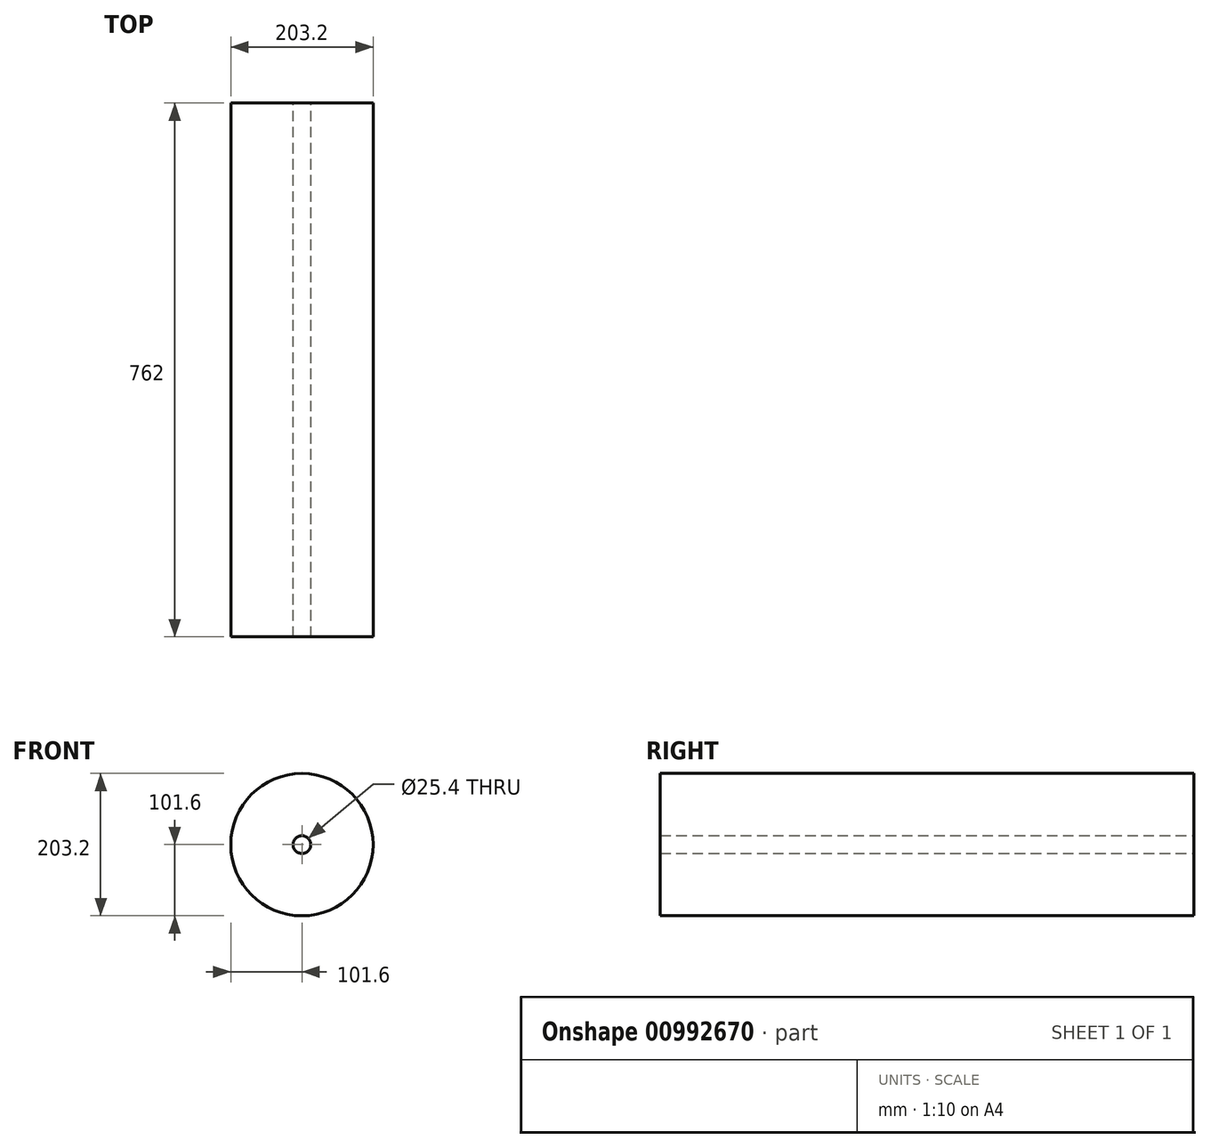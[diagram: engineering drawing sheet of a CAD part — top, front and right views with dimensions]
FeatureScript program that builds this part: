
annotation { "Feature Type Name" : "Feature", "Feature Type Description" : "" }
export const myFeature = defineFeature(function(context is Context, id is Id, definition is map)
    precondition{}
    {
        {
            var Q0;
            Q0=qCreatedBy(makeId("Front.planeOp"),FACE);
            var sketch = newSketch(context, id + "F0", { "sketchPlane" : qUnion([Q0])});
            skCircle(sketch, "E0", {"center": v(0, 0) * mm, "radius": 101.6 * mm});
            skCircle(sketch, "E1", {"center": v(0, 0) * mm, "radius": 12.7 * mm});
            skSolve(sketch);
        }
        {
            var Q0;
            Q0=makeQuery(id+"F0.imprint","IMPRINT",FACE,{"disambiguationData":[TD([[makeQuery(id+"F0.imprint","IMPRINT",EDGE,{"derivedFrom":sQuery(id+"F0.wireOp",EDGE,"E0")}),1.0]])]});
            extrude(context, id + "F1", {"entities" : qUnion([Q0]), "depth" : 762 * mm, "offsetDistance" : 25.4 * mm});
        }
    });
